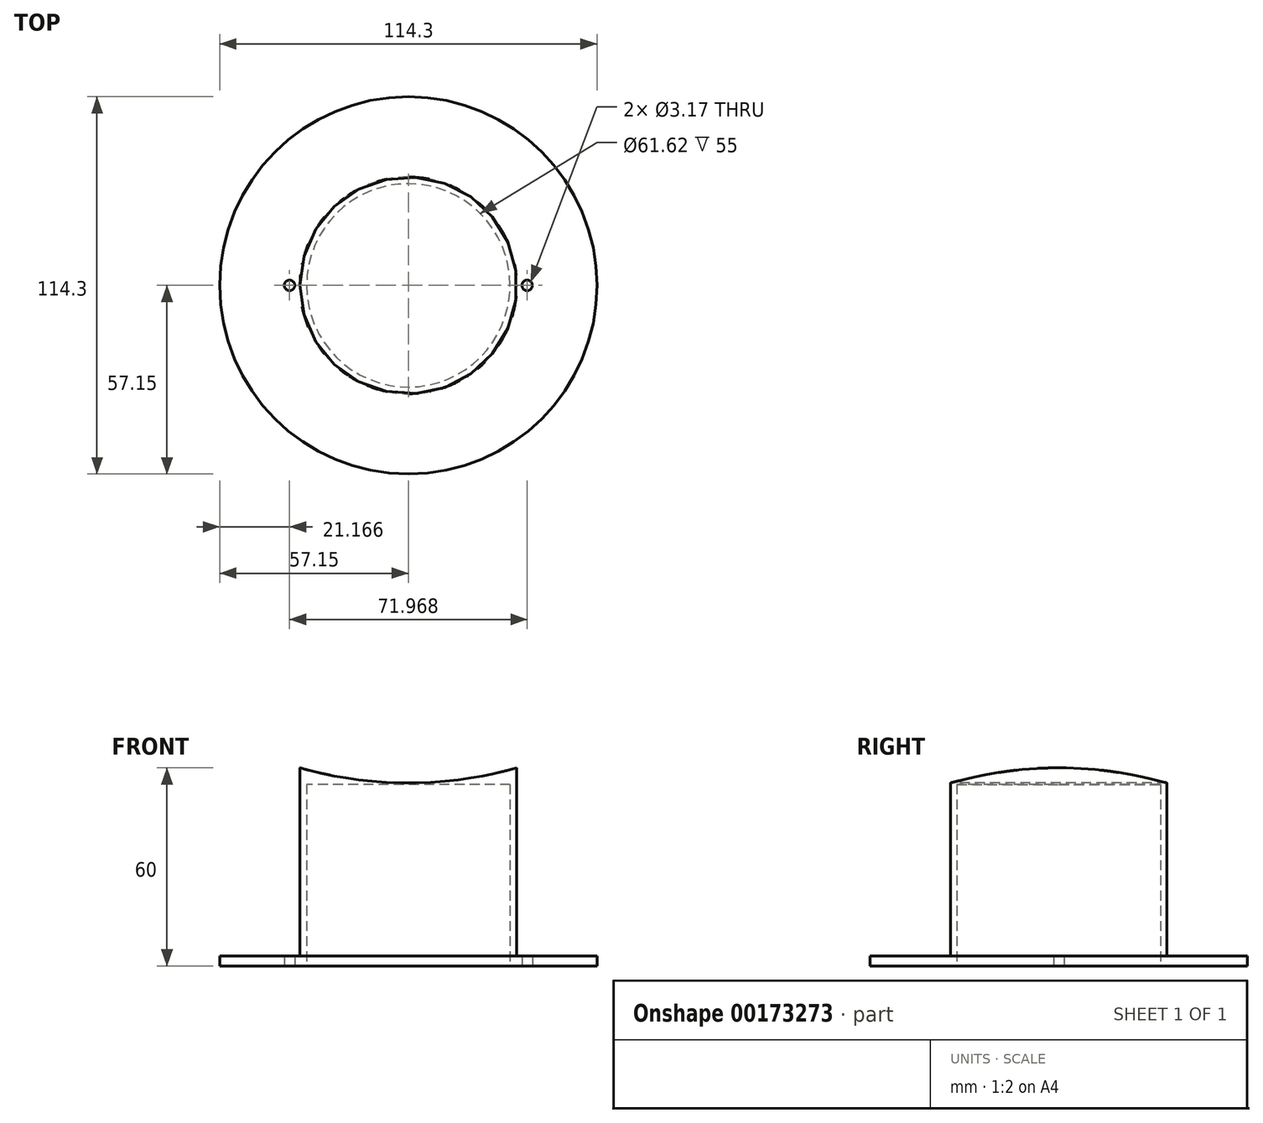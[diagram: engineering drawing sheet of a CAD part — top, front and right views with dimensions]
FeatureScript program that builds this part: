
annotation { "Feature Type Name" : "Feature", "Feature Type Description" : "" }
export const myFeature = defineFeature(function(context is Context, id is Id, definition is map)
    precondition{}
    {
        {
            var Q0;
            Q0=qCreatedBy(makeId("Top.planeOp"),FACE);
            var sketch = newSketch(context, id + "F0", { "sketchPlane" : qUnion([Q0])});
            skCircle(sketch, "E0", {"center": v(0, 0) * mm, "radius": 57.15 * mm});
            skCircle(sketch, "E1", {"center": v(0, 0) * mm, "radius": 32.8 * mm});
            skCircle(sketch, "E2", {"center": v(-35.98, 0) * mm, "radius": 1.59 * mm});
            skCircle(sketch, "E3", {"center": v(35.98, 0) * mm, "radius": 1.59 * mm});
            skCircle(sketch, "E4", {"center": v(0, 0) * mm, "radius": 30.8 * mm});
            skSolve(sketch);
        }
        {
            var Q0;
            Q0=makeQuery(id+"F0.imprint","IMPRINT",FACE,{"disambiguationData":[TD([[makeQuery(id+"F0.imprint","IMPRINT",EDGE,{"derivedFrom":sQuery(id+"F0.wireOp",EDGE,"E0")}),1.0]])]});
            extrude(context, id + "F1", {"entities" : qUnion([Q0]), "depth" : 3 * mm});
        }
        {
            var Q0;
            Q0=makeQuery(id+"F0.imprint","IMPRINT",FACE,{"disambiguationData":[TD([[makeQuery(id+"F0.imprint","IMPRINT",EDGE,{"derivedFrom":sQuery(id+"F0.wireOp",EDGE,"E1")}),1.0]])]});
            var Q1;
            Q1=makeQuery(id+"F0.imprint","IMPRINT",FACE,{"disambiguationData":[TD([[makeQuery(id+"F0.imprint","IMPRINT",EDGE,{"derivedFrom":sQuery(id+"F0.wireOp",EDGE,"E4")}),1.0]])]});
            extrude(context, id + "F2", {"entities" : qUnion([Q0, Q1]), "operationType" : NewBodyOperationType.ADD, "depth" : 60 * mm});
        }
        {
            var Q0;
            Q0=makeQuery(id+"F0.imprint","IMPRINT",FACE,{"disambiguationData":[TD([[makeQuery(id+"F0.imprint","IMPRINT",EDGE,{"derivedFrom":sQuery(id+"F0.wireOp",EDGE,"E4")}),1.0]])]});
            extrude(context, id + "F3", {"entities" : qUnion([Q0]), "operationType" : NewBodyOperationType.REMOVE, "depth" : 55 * mm});
        }
        {
            var Q0;
            Q0=qCreatedBy(makeId("Front.planeOp"),FACE);
            var sketch = newSketch(context, id + "F4", { "sketchPlane" : qUnion([Q0])});
            skLineSegment(sketch, "E5.0", {"start": v(-32.8, 60) * mm, "end": v(32.8, 60) * mm});
            skArc(sketch, "E6", {"start": v(-32.8, 60) * mm, "mid": v(0, 55.43) * mm, "end": v(32.8, 60) * mm});
            skSolve(sketch);
        }
        {
            var Q0;
            Q0 = qSketchRegion(id + "F4", true);
            extrude(context, id + "F5", {"entities" : qUnion([Q0]), "operationType" : NewBodyOperationType.REMOVE, "endBound" : BoundingType.SYMMETRIC, "oppositeDirection" : true, "depth" : 81 * mm});
        }
    });
